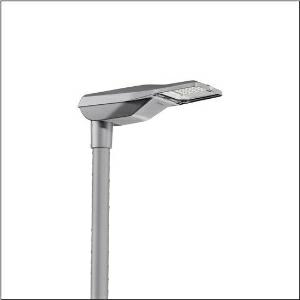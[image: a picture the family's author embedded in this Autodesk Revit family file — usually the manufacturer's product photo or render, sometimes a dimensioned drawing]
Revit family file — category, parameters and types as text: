
# Revit family: streetlight_sl_21_iq_micro___st0_8a_5xe1c41g08cb_fbf2
name_source: partatom
category: Lighting Fixtures
units: mm (PartAtom-declared; Revit-internal decimal feet)

## family parameters
Cut with Voids When Loaded = No
Host = Face
Light Source = No
Part Type = Normal
Room Calculation Point = No
Round Connector Dimension = Use Diameter
Shared = No

## types (1)
- --- (1 x LED, 2980 lm, 19.4 W, 4000K)
    Apparent Load = 19 VA
    CIE Flux Codes = 38 75 97 100 100
    Color Rendering = 70
    Color Temperature = 4000K
    Default Elevation = 1800 mm
    Description = Streetlight SL 21 iQ micro, mast luminaire, primary light control with lens, of PMMA, primary optical cover: cover, of toughened safety glass, transparent, light distribution: ST0.8a, light emission: direct distribution, primary light characteristic: asymmetric, installation type: post-top, side-entry, LED, High Power LED, rated luminous flux: 2.980lm, luminous efficacy: 154lm/W, light colour: 740, colour temperature: 4000K, control gear: iQ Street-Remote, control: Street-Remote, Auto-Match, Temp-Guard, Lumen-Switch, Night-Set, Smart-Wire, Light-Fading, Desk-Remote (wireless, voltage-free reading and setting of iQ features in the workshop via application-optimized NFC function/RFID function), optimised constant luminous flux control (CLO 2.0), pre-setting: linear dimming characteristic, mains connection: 220..240V, AC, 50/60Hz, start of lifetime: 19W, end of service life: 20W, reduction: 10W, luminaire housing, of diecast aluminium, powder-coated, SITECO metallic grey (DB 702S), corrosivity category C5 high according to DIN EN ISO 12944, please order mast flange separately, inclination adjustable: 0°, 5°, 10°, 15°, sealing non-destructively replaceable, multi-level sealing system, length: 528mm, width: 235mm, height: 110mm, mast flange for spigot size: 42mm (side-entry): 5XC10008XM4, 60/48mm (side-entry/post-top): 5XC10108XM2, 76/60mm (side-entry/post-top): 5XC10108XM1, protection rating (complete): IP66, insulation class (complete): insulation class II (safety insulation), certification: CE, ENEC, ENEC+, VDE, impact resistance: IK10, permissible operating ambient temperature for outdoor applications: -40..+50°C, standard-compliant lighting for roads and squares, packaging unit: 1 piece

Light Distribution: ST0.8a
    Height = 110 mm
    Lamp = 1 x LED
    Lamp Light Flux = 2980 lm
    Lamp Power = 19.4 W
    Lamp count = 1
    Length = 528 mm
    Luminous efficacy = 154 lm/W
    Manufacturer = Siteco
    ModVariant = No
    Model = 5XE1C41G08CB
    Number of Poles = 1
    OnlyDefault = Yes
    Power Factor = 1
    Product Name = Streetlight SL 21 iQ micro | ST0.8a
    Product group = mast luminaire | pylon top
    ProductGroupID = 6100
    Protection Class = Protection class II
    Protection Degree = IP 66
    RLX_Detail_Level = 1
    RLX_Emergency_Light_Flux = 0 lm
    RLX_Emergency_Type = 0
    RLX_Emergency_Type_DB = No
    RlxData = <blob elided: 98761 chars, md5=0e56af21>
    Socket = socket
    Standby Power = 0 W
    System Light Flux = 2980 lm
    System Power = 19 W
    Type Comments = factory setting: luminous flux: 100 % | dim-lin: 254 | 387 mA
    Type Image = l_1006881.jpg
    URL = http://relux.com
    VarID = @adj_137851
    Voltage = 0 V
    Weight = 0.00 kg
    Width = 235 mm

## geometry (parser evidence)
native form markers: Blend x4, Sweep x9
no freeform markers — native parametric forms only
